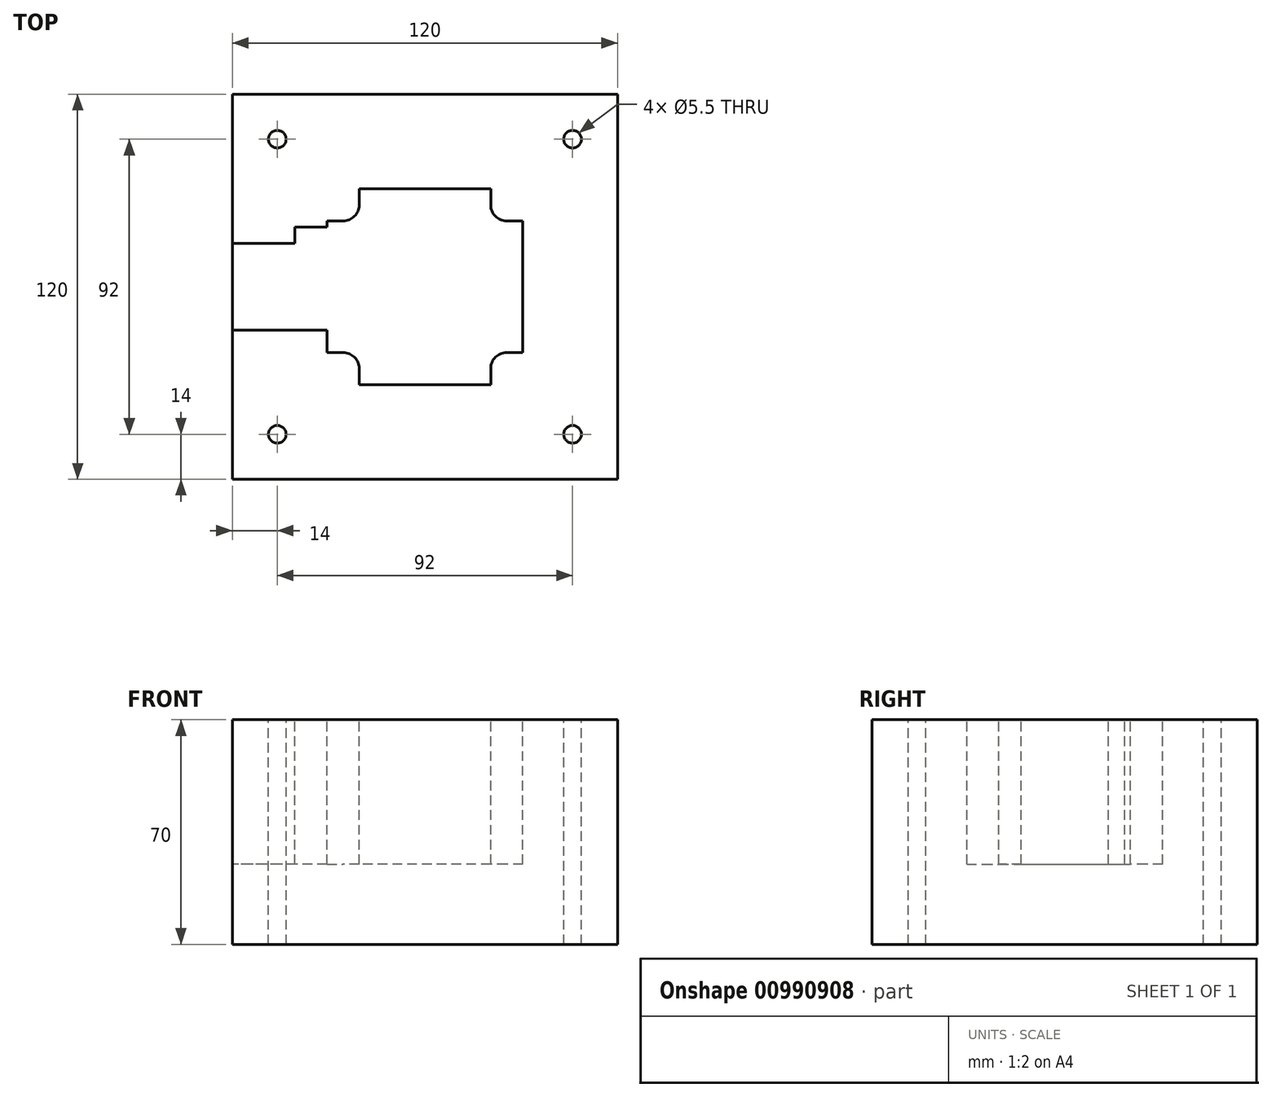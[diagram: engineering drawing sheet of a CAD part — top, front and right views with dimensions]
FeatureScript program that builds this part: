
annotation { "Feature Type Name" : "Feature", "Feature Type Description" : "" }
export const myFeature = defineFeature(function(context is Context, id is Id, definition is map)
    precondition{}
    {
        {
            var Q0;
            Q0=qCreatedBy(makeId("Top.planeOp"),FACE);
            var sketch = newSketch(context, id + "F0", { "sketchPlane" : qUnion([Q0])});
            skLineSegment(sketch, "E0.bottom", {"start": v(60, -60) * mm, "end": v(-60, -60) * mm});
            skLineSegment(sketch, "E0.top", {"start": v(60, 60) * mm, "end": v(-60, 60) * mm});
            skLineSegment(sketch, "E0.left", {"start": v(60, -60) * mm, "end": v(60, 60) * mm});
            skLineSegment(sketch, "E0.right", {"start": v(-60, -60) * mm, "end": v(-60, 60) * mm});
            skLineSegment(sketch, "E1.bottom", {"start": v(20.5, -30.5) * mm, "end": v(-20.5, -30.5) * mm});
            skLineSegment(sketch, "E1.top", {"start": v(20.5, 30.5) * mm, "end": v(-20.5, 30.5) * mm});
            skLineSegment(sketch, "E1.left", {"start": v(30.5, -20.5) * mm, "end": v(30.5, 20.5) * mm});
            skLineSegment(sketch, "E1.right", {"start": v(-30.5, -20.5) * mm, "end": v(-30.5, -18.65) * mm});
            skPoint(sketch, "E1.middle", {"position": v(0, 0) * mm});
            skLineSegment(sketch, "E2.top", {"start": v(-30.5, 20.5) * mm, "end": v(-25.5, 20.5) * mm});
            skLineSegment(sketch, "E2.right", {"start": v(-20.5, 30.5) * mm, "end": v(-20.5, 25.5) * mm});
            skLineSegment(sketch, "E3.MirrorCS", {"start": v(20.5, 30.5) * mm, "end": v(20.5, 25.5) * mm});
            skLineSegment(sketch, "E4.MirrorCS", {"start": v(30.5, 20.5) * mm, "end": v(25.5, 20.5) * mm});
            skLineSegment(sketch, "E5.MirrorCS", {"start": v(-30.5, -20.5) * mm, "end": v(-25.5, -20.5) * mm});
            skLineSegment(sketch, "E6.MirrorCS", {"start": v(-20.5, -30.5) * mm, "end": v(-20.5, -25.5) * mm});
            skLineSegment(sketch, "E7.MirrorCS", {"start": v(20.5, -30.5) * mm, "end": v(20.5, -25.5) * mm});
            skLineSegment(sketch, "E8.MirrorCS", {"start": v(30.5, -20.5) * mm, "end": v(25.5, -20.5) * mm});
            skPoint(sketch, "E9.orphan", {"position": v(-30.5, 30.5) * mm});
            skPoint(sketch, "E10.orphan", {"position": v(30.5, 30.5) * mm});
            skPoint(sketch, "E11.orphan", {"position": v(30.5, -30.5) * mm});
            skPoint(sketch, "E12.orphan", {"position": v(-30.5, -30.5) * mm});
            skLineSegment(sketch, "E13.bottom", {"start": v(-40.5, -13.55) * mm, "end": v(-60, -13.55) * mm});
            skLineSegment(sketch, "E13.top", {"start": v(-30.5, 13.55) * mm, "end": v(-60, 13.55) * mm});
            skLineSegment(sketch, "E13.left", {"start": v(-30.5, -13.55) * mm, "end": v(-30.5, 13.55) * mm});
            skLineSegment(sketch, "E13.right", {"start": v(-60, -13.55) * mm, "end": v(-60, 13.55) * mm});
            skPoint(sketch, "E13.middle", {"position": v(-45.25, 0) * mm});
            skPoint(sketch, "E14.visualSharp", {"position": v(-20.5, 20.5) * mm});
            skArc(sketch, "E14.filletArc", {"start": v(-25.5, 20.5) * mm, "mid": v(-21.96, 21.96) * mm, "end": v(-20.5, 25.5) * mm});
            skPoint(sketch, "E15.visualSharp", {"position": v(20.5, 20.5) * mm});
            skArc(sketch, "E15.filletArc", {"start": v(20.5, 25.5) * mm, "mid": v(21.96, 21.96) * mm, "end": v(25.5, 20.5) * mm});
            skPoint(sketch, "E16.visualSharp", {"position": v(20.5, -20.5) * mm});
            skArc(sketch, "E16.filletArc", {"start": v(25.5, -20.5) * mm, "mid": v(21.96, -21.96) * mm, "end": v(20.5, -25.5) * mm});
            skPoint(sketch, "E17.visualSharp", {"position": v(-20.5, -20.5) * mm});
            skArc(sketch, "E17.filletArc", {"start": v(-20.5, -25.5) * mm, "mid": v(-21.96, -21.96) * mm, "end": v(-25.5, -20.5) * mm});
            skLineSegment(sketch, "E18.bottom", {"start": v(-30.5, -13.55) * mm, "end": v(-60, -13.55) * mm});
            skLineSegment(sketch, "E18.left", {"start": v(-30.5, -13.55) * mm, "end": v(-30.5, -18.65) * mm});
            skLineSegment(sketch, "E18.right", {"start": v(-60, -13.55) * mm, "end": v(-60, -18.65) * mm});
            skLineSegment(sketch, "E19.MirrorCS", {"start": v(-40.5, 13.55) * mm, "end": v(-40.5, 18.65) * mm});
            skLineSegment(sketch, "E20.MirrorCS", {"start": v(-30.5, 18.65) * mm, "end": v(-40.5, 18.65) * mm});
            skPoint(sketch, "E21.top.end.orphan", {"position": v(-40.5, -18.65) * mm});
            skLineSegment(sketch, "E22.trimOffspring", {"start": v(-30.5, -13.55) * mm, "end": v(-30.5, 20.5) * mm});
            skCircle(sketch, "E23", {"center": v(-46, 46) * mm, "radius": 2.75 * mm});
            skCircle(sketch, "E24.MirrorC", {"center": v(46, 46) * mm, "radius": 2.75 * mm});
            skCircle(sketch, "E25.MirrorC", {"center": v(-46, -46) * mm, "radius": 2.75 * mm});
            skCircle(sketch, "E26.MirrorC", {"center": v(46, -46) * mm, "radius": 2.75 * mm});
            skSolve(sketch);
        }
        {
            var Q0;
            {var subQ1=sQuery(id+"F0.wireOp",EDGE,"E0.bottom");Q0=makeQuery(id+"F0.imprint","IMPRINT",FACE,{"disambiguationData":[TD([[makeQuery(id+"F0.imprint","IMPRINT",EDGE,{"derivedFrom":subQ1}),-1.0]])]});}
            var Q1;
            Q1=makeQuery(id+"F0.imprint","IMPRINT",FACE,{"disambiguationData":[TD([[makeQuery(id+"F0.imprint","IMPRINT",EDGE,{"derivedFrom":sQuery(id+"F0.wireOp",EDGE,"SYu9wuvn-9oXB-xavs-NCNW-ztSgYm0V7tR3.bottom")}),-1.0]])]});
            var Q2;
            {var subQ6=sQuery(id+"F0.wireOp",EDGE,"E13.top");Q2=makeQuery(id+"F0.imprint","IMPRINT",FACE,{"disambiguationData":[TD([[makeQuery(id+"F0.imprint","IMPRINT",EDGE,{"derivedFrom":subQ6}),1.0]])]});}
            var Q3;
            Q3=makeQuery(id+"F0.imprint","IMPRINT",FACE,{"disambiguationData":[TD([[makeQuery(id+"F0.imprint","IMPRINT",EDGE,{"derivedFrom":sQuery(id+"F0.wireOp",EDGE,"E1.bottom")}),-1.0]])]});
            var Q4;
            {var subQ3=sQuery(id+"F0.wireOp",EDGE,"E21.top");Q4=makeQuery(id+"F0.imprint","IMPRINT",FACE,{"disambiguationData":[TD([[makeQuery(id+"F0.imprint","IMPRINT",EDGE,{"derivedFrom":subQ3}),-1.0]])]});}
            var Q5;
            {var subQ0=sQuery(id+"F0.wireOp",EDGE,"E19.MirrorCS");Q5=makeQuery(id+"F0.imprint","IMPRINT",FACE,{"disambiguationData":[TD([[makeQuery(id+"F0.imprint","IMPRINT",EDGE,{"derivedFrom":subQ0}),-1.0]])]});}
            extrude(context, id + "F1", {"entities" : qUnion([Q0, Q1, Q2, Q3, Q4, Q5]), "oppositeDirection" : true, "depth" : 70 * mm, "offsetDistance" : 25 * mm});
        }
        {
            var Q0;
            Q0=makeQuery(id+"F0.imprint","IMPRINT",FACE,{"disambiguationData":[TD([[makeQuery(id+"F0.imprint","IMPRINT",EDGE,{"derivedFrom":sQuery(id+"F0.wireOp",EDGE,"SYu9wuvn-9oXB-xavs-NCNW-ztSgYm0V7tR3.bottom")}),-1.0]])]});
            var Q1;
            {var subQ6=sQuery(id+"F0.wireOp",EDGE,"E13.top");Q1=makeQuery(id+"F0.imprint","IMPRINT",FACE,{"disambiguationData":[TD([[makeQuery(id+"F0.imprint","IMPRINT",EDGE,{"derivedFrom":subQ6}),1.0]])]});}
            var Q2;
            {var subQ3=sQuery(id+"F0.wireOp",EDGE,"E21.top");Q2=makeQuery(id+"F0.imprint","IMPRINT",FACE,{"disambiguationData":[TD([[makeQuery(id+"F0.imprint","IMPRINT",EDGE,{"derivedFrom":subQ3}),-1.0]])]});}
            var Q3;
            Q3=makeQuery(id+"F0.imprint","IMPRINT",FACE,{"disambiguationData":[TD([[makeQuery(id+"F0.imprint","IMPRINT",EDGE,{"derivedFrom":sQuery(id+"F0.wireOp",EDGE,"E1.bottom")}),-1.0]])]});
            var Q4;
            {var subQ0=sQuery(id+"F0.wireOp",EDGE,"E19.MirrorCS");Q4=makeQuery(id+"F0.imprint","IMPRINT",FACE,{"disambiguationData":[TD([[makeQuery(id+"F0.imprint","IMPRINT",EDGE,{"derivedFrom":subQ0}),-1.0]])]});}
            extrude(context, id + "F2", {"entities" : qUnion([Q0, Q1, Q2, Q3, Q4]), "operationType" : NewBodyOperationType.REMOVE, "oppositeDirection" : true, "depth" : 45 * mm, "offsetDistance" : 25 * mm});
        }
    });
